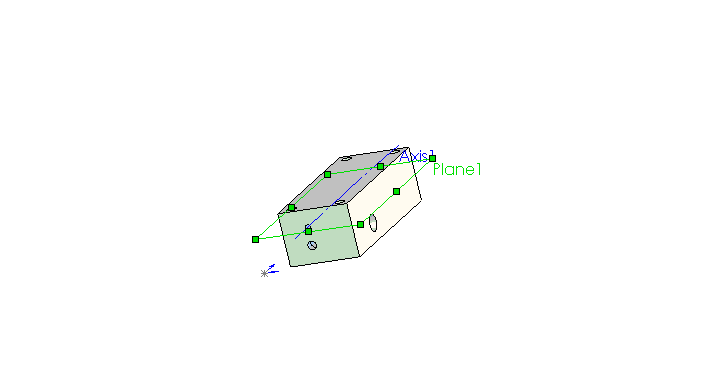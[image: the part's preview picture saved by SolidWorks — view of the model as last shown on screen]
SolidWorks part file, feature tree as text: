
SOLIDWORKS PART (.sldprt)
format: sldprt  version: not decoded by parser v0  size: 151,040 bytes
history: native  units: mm
features: sketch x6, cut_extrude x5, extrude x1, plane x1 (+11 scaffold rows collapsed)
feature tree (24):
  scaffold x11  (default folders/planes/origin — collapsed)
  sketch  "Sketch1"  dims[D1=66.675mm D2=25.4mm]
  extrude  "Extrude1"  Depth=19.05mm
  sketch  "Sketch2"  dims[D1=6.35mm D2=9.525mm D3=6.35mm]
  cut_extrude  "Cut-Extrude1"  Depth=63.5mm
  sketch  "Sketch3"  dims[D1=3.175mm D2=6.35mm]
  cut_extrude  "Cut-Extrude2"  [1 undecoded]
  sketch  "Sketch4"  dims[D1=6.35mm D2=19.05mm]
  cut_extrude  "Cut-Extrude3"  Depth=10.16mm
  sketch  "Sketch5"  dims[c1.D1=3.4925mm c1.D4=3.4925mm c1.D6=3.4925mm c1.D2=3.81mm c1.D3=3.81mm c1.D5=3.81mm c2.D6=33.3375mm]
  cut_extrude  "Cut-Extrude4"  [1 undecoded]
  sketch  "Sketch6"  dims[D1=2.1082mm D2=6.35mm]
  cut_extrude  "Cut-Extrude6"  [1 undecoded]
  plane  "Plane1"  Offset=12.7mm
decode coverage: 9 of 12 modeling features carry decoded parameters
note: 3 parameter values undecoded
summary: no parameter record found for 3 features
note: suppression state not decoded; provenance and decode notes live in map.json
